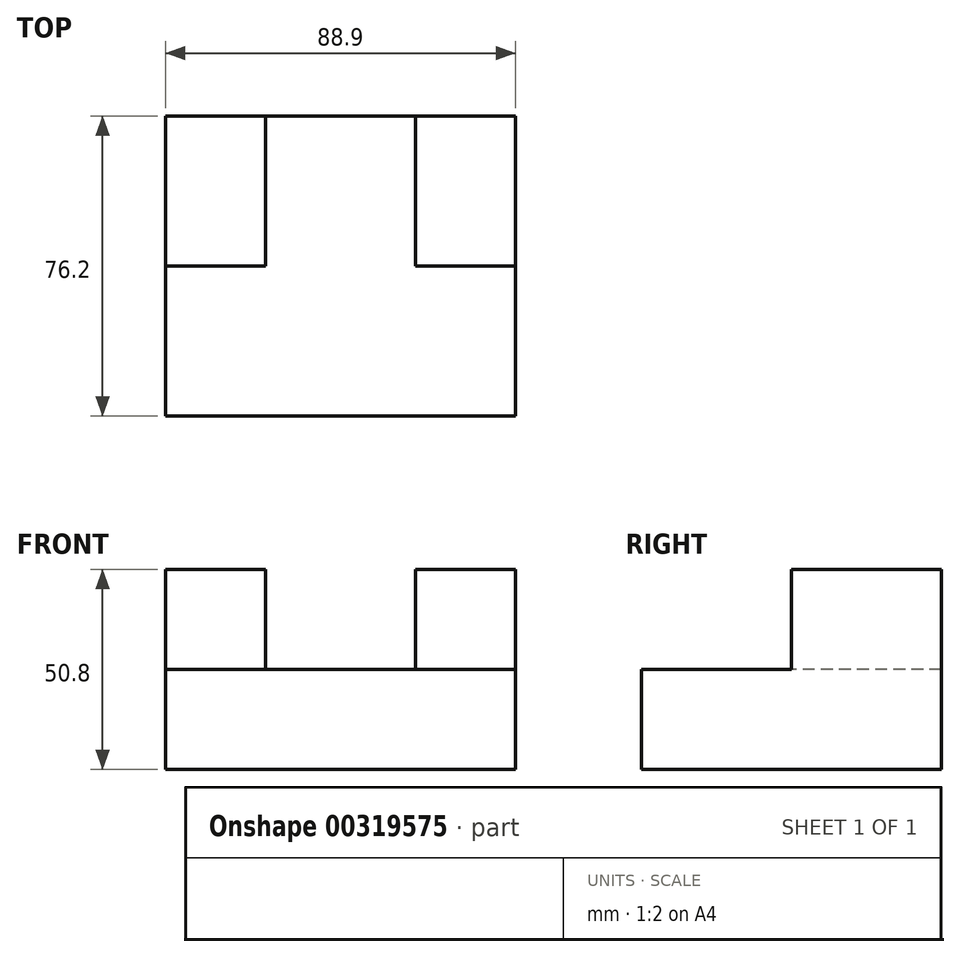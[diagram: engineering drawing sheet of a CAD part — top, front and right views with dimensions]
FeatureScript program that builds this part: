
annotation { "Feature Type Name" : "Feature", "Feature Type Description" : "" }
export const myFeature = defineFeature(function(context is Context, id is Id, definition is map)
    precondition{}
    {
        {
            var Q0;
            Q0=qCreatedBy(makeId("Front.planeOp"),FACE);
            var sketch = newSketch(context, id + "F0", { "sketchPlane" : qUnion([Q0])});
            skLineSegment(sketch, "E0", {"start": v(-66.56, -53.71) * mm, "end": v(22.34, -53.71) * mm});
            skLineSegment(sketch, "E1", {"start": v(22.34, -53.71) * mm, "end": v(22.34, -28.31) * mm});
            skLineSegment(sketch, "E2", {"start": v(22.34, -28.31) * mm, "end": v(-66.56, -28.31) * mm});
            skLineSegment(sketch, "E3", {"start": v(-66.56, -28.31) * mm, "end": v(-66.56, -53.71) * mm});
            skSolve(sketch);
        }
        {
            var Q0;
            Q0=makeQuery(id+"F0.imprint","IMPRINT",FACE,{"disambiguationData":[TD([[makeQuery(id+"F0.imprint","IMPRINT",EDGE,{"derivedFrom":sQuery(id+"F0.wireOp",EDGE,"E0")}),1.0]])]});
            extrude(context, id + "F1", {"entities" : qUnion([Q0]), "depth" : 76.2 * mm});
        }
        {
            var Q0;
            Q0=makeQuery(id+"F1.opExtrude","SWEPT_FACE",FACE,{"disambiguationData":[OSD([sQuery(id+"F0.wireOp",EDGE,"E2")])]});
            var sketch = newSketch(context, id + "F2", { "sketchPlane" : qUnion([Q0])});
            skLineSegment(sketch, "E4", {"start": v(22.34, 0) * mm, "end": v(-3.06, 0) * mm});
            skLineSegment(sketch, "E5", {"start": v(-3.06, 0) * mm, "end": v(-3.06, -38.1) * mm});
            skLineSegment(sketch, "E6", {"start": v(-3.06, -38.1) * mm, "end": v(22.34, -38.1) * mm});
            skLineSegment(sketch, "E7", {"start": v(22.34, -38.1) * mm, "end": v(22.34, 0) * mm});
            skLineSegment(sketch, "E8", {"start": v(-66.56, 0) * mm, "end": v(-66.56, -38.1) * mm});
            skLineSegment(sketch, "E9", {"start": v(-66.56, -38.1) * mm, "end": v(-41.16, -38.1) * mm});
            skLineSegment(sketch, "E10", {"start": v(-41.16, -38.1) * mm, "end": v(-41.16, 0) * mm});
            skLineSegment(sketch, "E11", {"start": v(-41.16, 0) * mm, "end": v(-66.56, 0) * mm});
            skSolve(sketch);
        }
        {
            var Q0;
            Q0=makeQuery(id+"F2.imprint","IMPRINT",FACE,{"disambiguationData":[TD([[makeQuery(id+"F2.imprint","IMPRINT",EDGE,{"derivedFrom":sQuery(id+"F2.wireOp",EDGE,"E8")}),-1.0]])]});
            extrude(context, id + "F3", {"entities" : qUnion([Q0]), "operationType" : NewBodyOperationType.ADD, "depth" : 25.4 * mm});
        }
        {
            var Q0;
            Q0 = qSketchRegion(id + "F2", true);
            extrude(context, id + "F4", {"entities" : qUnion([Q0]), "operationType" : NewBodyOperationType.ADD, "depth" : 25.4 * mm});
        }
    });
